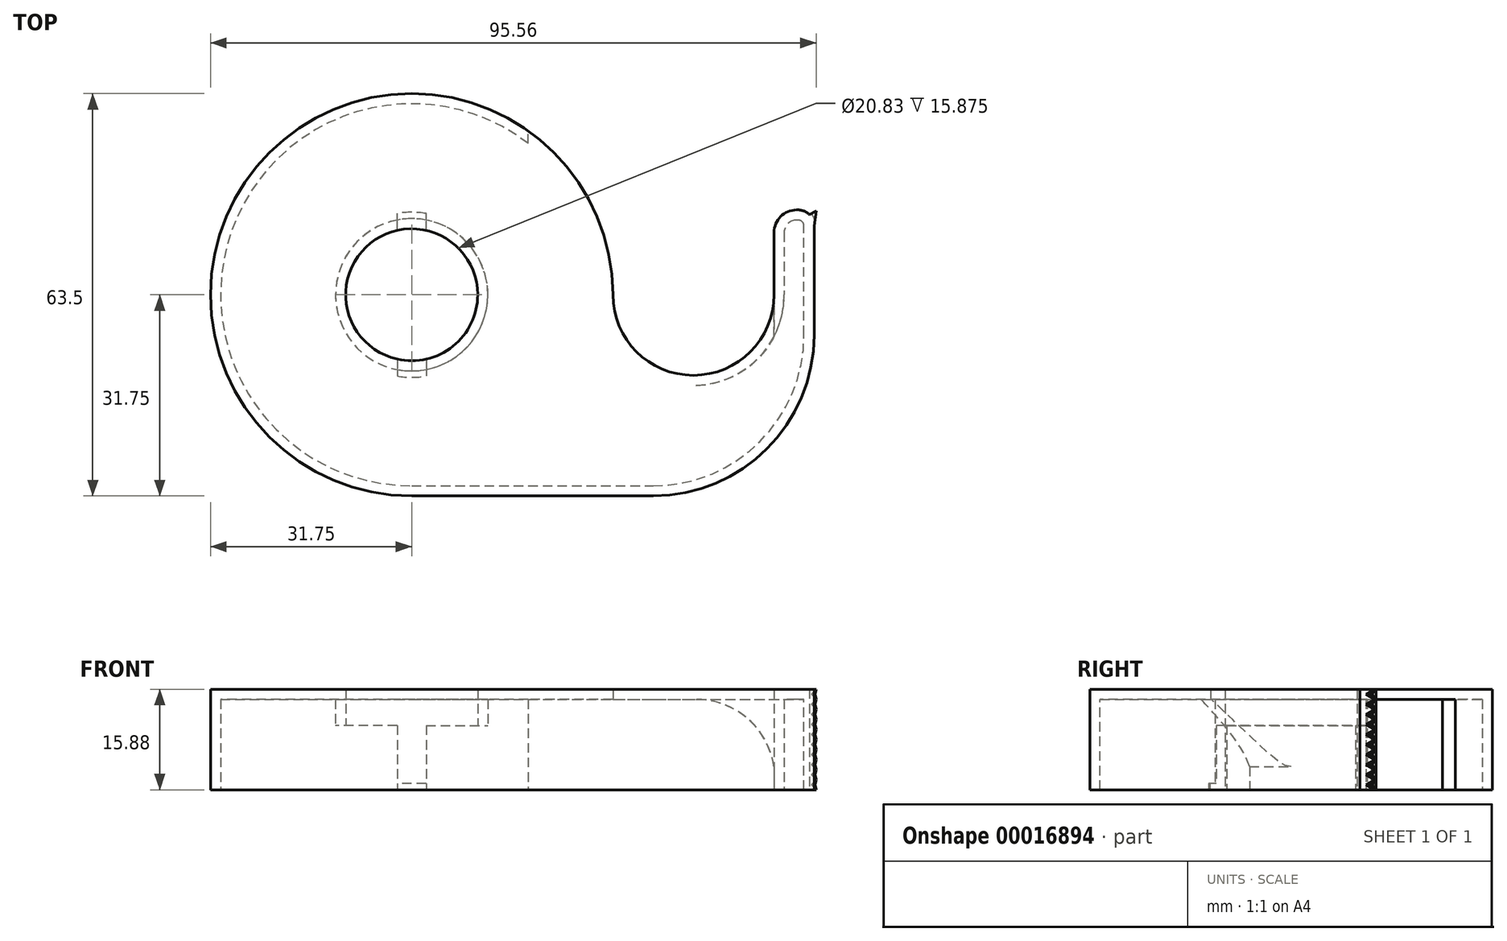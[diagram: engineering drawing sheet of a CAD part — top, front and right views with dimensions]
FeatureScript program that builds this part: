
annotation { "Feature Type Name" : "Feature", "Feature Type Description" : "" }
export const myFeature = defineFeature(function(context is Context, id is Id, definition is map)
    precondition{}
    {
        {
            var Q0;
            Q0=qCreatedBy(makeId("Top.planeOp"),FACE);
            var sketch = newSketch(context, id + "F0", { "sketchPlane" : qUnion([Q0])});
            skCircle(sketch, "E0", {"center": v(0, 0) * mm, "radius": 10.41 * mm});
            skArc(sketch, "E1", {"start": v(31.75, 0) * mm, "mid": v(-22.45, 22.45) * mm, "end": v(0, -31.75) * mm});
            skLineSegment(sketch, "E2", {"start": v(-31.75, 0) * mm, "end": v(31.75, 0) * mm, "construction": true});
            skLineSegment(sketch, "E3", {"start": v(0, -31.75) * mm, "end": v(38.1, -31.75) * mm});
            skLineSegment(sketch, "E4", {"start": v(63.5, -6.35) * mm, "end": v(63.5, 10.85) * mm});
            skLineSegment(sketch, "E5", {"start": v(60.96, 13.4) * mm, "end": v(60.73, 13.4) * mm});
            skLineSegment(sketch, "E6", {"start": v(57.17, 9.83) * mm, "end": v(57.17, 0) * mm});
            skArc(sketch, "E7", {"start": v(57.17, 0) * mm, "mid": v(44.46, -12.71) * mm, "end": v(31.75, 0) * mm});
            skLineSegment(sketch, "E8.trimOffspring", {"start": v(57.17, 13.4) * mm, "end": v(63.5, 13.4) * mm, "construction": true});
            skPoint(sketch, "E9.start.orphan", {"position": v(0, 10.41) * mm});
            skPoint(sketch, "E10.visualSharp", {"position": v(63.5, -31.75) * mm});
            skArc(sketch, "E10.filletArc", {"start": v(38.1, -31.75) * mm, "mid": v(56.06, -24.31) * mm, "end": v(63.5, -6.35) * mm});
            skPoint(sketch, "E11.visualSharp", {"position": v(63.5, 13.4) * mm});
            skArc(sketch, "E11.filletArc", {"start": v(62.76, 12.65) * mm, "mid": v(61.93, 13.2) * mm, "end": v(60.96, 13.4) * mm});
            skPoint(sketch, "E12.visualSharp", {"position": v(57.17, 13.4) * mm});
            skArc(sketch, "E12.filletArc", {"start": v(60.73, 13.4) * mm, "mid": v(58.21, 12.35) * mm, "end": v(57.17, 9.83) * mm});
            skLineSegment(sketch, "E13", {"start": v(63.5, 10.85) * mm, "end": v(63.8, 13.21) * mm});
            skLineSegment(sketch, "E14", {"start": v(63.8, 13.21) * mm, "end": v(62.76, 12.65) * mm});
            skSolve(sketch);
        }
        {
            var Q0;
            Q0=makeQuery(id+"F0.imprint","IMPRINT",FACE,{"disambiguationData":[TD([[makeQuery(id+"F0.imprint","IMPRINT",EDGE,{"derivedFrom":sQuery(id+"F0.wireOp",EDGE,"E0")}),-1.0]])]});
            extrude(context, id + "F1", {"entities" : qUnion([Q0]), "depth" : 15.88 * mm});
        }
        {
            var Q0;
            Q0=makeQuery(id+"F1.opExtrude","CAP_FACE",FACE,{"disambiguationData":[OSD([sQuery(id+"F0.wireOp",EDGE,"E0"),sQuery(id+"F0.wireOp",EDGE,"E1"),sQuery(id+"F0.wireOp",EDGE,"E3"),sQuery(id+"F0.wireOp",EDGE,"E4"),sQuery(id+"F0.wireOp",EDGE,"E5"),sQuery(id+"F0.wireOp",EDGE,"E6"),sQuery(id+"F0.wireOp",EDGE,"E7"),sQuery(id+"F0.wireOp",EDGE,"E10.filletArc")])],"isStart":true});
            shell(context, id + "F2", {"entities" : qUnion([Q0]), "thickness" : 1.6 * mm});
        }
        {
            var Q0;
            Q0=qCreatedBy(makeId("Front.planeOp"),FACE);
            cPlane(context, id + "F3", {"entities" : qUnion([Q0]), "cplaneType" : CPlaneType.OFFSET, "offset" : 38.1 * mm, "oppositeDirection" : true, "width" : 152.4 * mm, "height" : 152.4 * mm});
        }
        {
            var Q0;
            Q0=qCreatedBy(id+"F3.planeOp",FACE);
            var sketch = newSketch(context, id + "F4", { "sketchPlane" : qUnion([Q0])});
            skLineSegment(sketch, "E15.0", {"start": v(57.17, 15.88) * mm, "end": v(57.17, 0) * mm, "construction": true});
            skLineSegment(sketch, "E16.0", {"start": v(58.77, 14.27) * mm, "end": v(30.15, 14.27) * mm, "construction": true});
            skLineSegment(sketch, "E17.0", {"start": v(-30.15, 14.27) * mm, "end": v(30.15, 14.27) * mm, "construction": true});
            skLineSegment(sketch, "E18", {"start": v(18.4, 14.27) * mm, "end": v(18.4, -5.65) * mm});
            skLineSegment(sketch, "E19", {"start": v(18.4, -5.65) * mm, "end": v(57.17, -5.65) * mm});
            skLineSegment(sketch, "E20", {"start": v(18.4, 14.27) * mm, "end": v(44.86, 14.27) * mm});
            skArc(sketch, "E21", {"start": v(44.86, 14.27) * mm, "mid": v(53, 11.25) * mm, "end": v(57.17, 3.65) * mm});
            skLineSegment(sketch, "E22", {"start": v(57.17, 3.65) * mm, "end": v(57.17, -5.65) * mm});
            skSolve(sketch);
        }
        {
            var Q0;
            Q0 = qSketchRegion(id + "F4", true);
            extrude(context, id + "F5", {"entities" : qUnion([Q0]), "operationType" : NewBodyOperationType.REMOVE, "depth" : 53.45 * mm});
        }
        {
            var Q0;
            Q0=qCreatedBy(makeId("Top.planeOp"),FACE);
            var sketch = newSketch(context, id + "F6", { "sketchPlane" : qUnion([Q0])});
            skCircle(sketch, "E23.0", {"center": v(0, 0) * mm, "radius": 10.41 * mm});
            skLineSegment(sketch, "E24", {"start": v(-2.29, 12.7) * mm, "end": v(-2.29, 16.7) * mm});
            skLineSegment(sketch, "E25", {"start": v(-2.29, 16.7) * mm, "end": v(-16.67, 16.7) * mm});
            skLineSegment(sketch, "E26", {"start": v(0, 0) * mm, "end": v(0, 5.96) * mm});
            skLineSegment(sketch, "E27", {"start": v(0, 0) * mm, "end": v(-8.58, 0) * mm});
            skLineSegment(sketch, "E28", {"start": v(-16.67, 16.7) * mm, "end": v(-16.67, 0) * mm});
            skLineSegment(sketch, "E29", {"start": v(-2.29, 10.16) * mm, "end": v(-2.29, 12.7) * mm});
            skPoint(sketch, "E30.start.orphan", {"position": v(0, 10.41) * mm});
            skLineSegment(sketch, "E31.MirrorCS", {"start": v(2.29, 12.7) * mm, "end": v(2.29, 16.7) * mm});
            skLineSegment(sketch, "E32.MirrorCS", {"start": v(2.29, 16.7) * mm, "end": v(16.67, 16.7) * mm});
            skLineSegment(sketch, "E33.MirrorCS", {"start": v(16.67, 16.7) * mm, "end": v(16.67, 0) * mm});
            skLineSegment(sketch, "E34.MirrorCS", {"start": v(2.29, 10.16) * mm, "end": v(2.29, 12.7) * mm});
            skLineSegment(sketch, "E35.MirrorCS", {"start": v(-2.29, -12.7) * mm, "end": v(-2.29, -16.7) * mm});
            skLineSegment(sketch, "E36.MirrorCS", {"start": v(-2.29, -16.7) * mm, "end": v(-16.67, -16.7) * mm});
            skLineSegment(sketch, "E37.MirrorCS", {"start": v(-16.67, -16.7) * mm, "end": v(-16.67, 0) * mm});
            skLineSegment(sketch, "E38.MirrorCS", {"start": v(-2.29, -10.16) * mm, "end": v(-2.29, -12.7) * mm});
            skLineSegment(sketch, "E39.MirrorCS", {"start": v(16.67, -16.7) * mm, "end": v(16.67, 0) * mm});
            skLineSegment(sketch, "E40.MirrorCS", {"start": v(2.29, -16.7) * mm, "end": v(16.67, -16.7) * mm});
            skLineSegment(sketch, "E41.MirrorCS", {"start": v(2.29, -12.7) * mm, "end": v(2.29, -16.7) * mm});
            skLineSegment(sketch, "E42.MirrorCS", {"start": v(2.29, -10.16) * mm, "end": v(2.29, -12.7) * mm});
            skSolve(sketch);
        }
        {
            var Q0;
            Q0 = qSketchRegion(id + "F6", true);
            extrude(context, id + "F7", {"entities" : qUnion([Q0]), "operationType" : NewBodyOperationType.REMOVE, "depth" : 10.16 * mm});
        }
        {
            var Q0;
            {var subQ0=sQuery(id+"F0.wireOp",EDGE,"E0");var subQ1=sQuery(id+"F0.wireOp",EDGE,"E1");var subQ2=sQuery(id+"F0.wireOp",EDGE,"E3");var subQ3=sQuery(id+"F0.wireOp",EDGE,"E4");var subQ4=sQuery(id+"F0.wireOp",EDGE,"E5");var subQ5=sQuery(id+"F0.wireOp",EDGE,"E6");var subQ6=sQuery(id+"F0.wireOp",EDGE,"E7");var subQ7=sQuery(id+"F0.wireOp",EDGE,"E10.filletArc");Q0=makeQuery(id+"F7.boolean.opBoolean","SPLIT",FACE,{"disambiguationData":[TD([makeQuery(id+"F7.opExtrude","SWEPT_FACE",FACE,{"disambiguationData":[OSD([sQuery(id+"F6.wireOp",EDGE,"E35.MirrorCS"),sQuery(id+"F6.wireOp",EDGE,"E38.MirrorCS")])]})])],"derivedFrom":makeQuery(id+"F2.opShell","OFFSET_FACE",FACE,{"disambiguationData":[OSD([subQ0,subQ1,subQ2,subQ3,subQ4,subQ5,subQ6,subQ7]),TDD([makeQuery(id+"F1.opExtrude","CAP_FACE",FACE,{"disambiguationData":[OSD([subQ0,subQ1,subQ2,subQ3,subQ4,subQ5,subQ6,subQ7])],"isStart":true})])]})});}
            var sketch = newSketch(context, id + "F8", { "sketchPlane" : qUnion([Q0])});
            skLineSegment(sketch, "E43", {"start": v(-2.29, 11.8) * mm, "end": v(-2.29, 12.83) * mm});
            skLineSegment(sketch, "E44", {"start": v(2.29, 11.8) * mm, "end": v(2.29, 12.83) * mm});
            skArc(sketch, "E45.0", {"start": v(-2.29, 11.8) * mm, "mid": v(0, 12.01) * mm, "end": v(2.29, 11.8) * mm});
            skArc(sketch, "E46.0", {"start": v(-2.29, 12.83) * mm, "mid": v(0, 13.03) * mm, "end": v(2.29, 12.83) * mm});
            skLineSegment(sketch, "E47", {"start": v(0, 0) * mm, "end": v(-7.46, 0) * mm, "construction": true});
            skLineSegment(sketch, "E48.MirrorCS", {"start": v(2.29, -11.8) * mm, "end": v(2.29, -12.83) * mm});
            skArc(sketch, "E49.MirrorCS", {"start": v(-2.29, -12.83) * mm, "mid": v(0, -13.03) * mm, "end": v(2.29, -12.83) * mm});
            skLineSegment(sketch, "E50.MirrorCS", {"start": v(-2.29, -11.8) * mm, "end": v(-2.29, -12.83) * mm});
            skArc(sketch, "E51.MirrorCS", {"start": v(-2.29, -11.8) * mm, "mid": v(0, -12.01) * mm, "end": v(2.29, -11.8) * mm});
            skSolve(sketch);
        }
        {
            var Q0;
            Q0 = qSketchRegion(id + "F8", true);
            extrude(context, id + "F9", {"entities" : qUnion([Q0]), "operationType" : NewBodyOperationType.ADD, "oppositeDirection" : true, "depth" : 1.02 * mm});
        }
        {
            var Q0;
            Q0=makeQuery(id+"F1.opExtrude","SWEPT_FACE",FACE,{"disambiguationData":[OSD([sQuery(id+"F0.wireOp",EDGE,"E14")])]});
            var sketch = newSketch(context, id + "F10", { "sketchPlane" : qUnion([Q0])});
            skLineSegment(sketch, "E52", {"start": v(-62.5, 0) * mm, "end": v(-62.5, 1.59) * mm});
            skLineSegment(sketch, "E53", {"start": v(-62.5, 1.59) * mm, "end": v(-61.68, 0.8) * mm});
            skLineSegment(sketch, "E54", {"start": v(-61.68, 0.8) * mm, "end": v(-62.5, 0) * mm});
            skLineSegment(sketch, "E55.0.1.0", {"start": v(-62.5, 3.17) * mm, "end": v(-61.68, 2.38) * mm});
            skLineSegment(sketch, "E55.0.1.1", {"start": v(-61.68, 2.38) * mm, "end": v(-62.5, 1.59) * mm});
            skLineSegment(sketch, "E55.0.1.2", {"start": v(-62.5, 1.59) * mm, "end": v(-62.5, 3.18) * mm});
            skLineSegment(sketch, "E55.0.2.0", {"start": v(-62.5, 4.76) * mm, "end": v(-61.68, 3.97) * mm});
            skLineSegment(sketch, "E55.0.2.1", {"start": v(-61.68, 3.97) * mm, "end": v(-62.5, 3.18) * mm});
            skLineSegment(sketch, "E55.0.2.2", {"start": v(-62.5, 3.18) * mm, "end": v(-62.5, 4.76) * mm});
            skLineSegment(sketch, "E55.0.3.0", {"start": v(-62.5, 6.35) * mm, "end": v(-61.68, 5.56) * mm});
            skLineSegment(sketch, "E55.0.3.1", {"start": v(-61.68, 5.56) * mm, "end": v(-62.5, 4.76) * mm});
            skLineSegment(sketch, "E55.0.3.2", {"start": v(-62.5, 4.76) * mm, "end": v(-62.5, 6.35) * mm});
            skLineSegment(sketch, "E55.0.4.0", {"start": v(-62.5, 7.94) * mm, "end": v(-61.68, 7.14) * mm});
            skLineSegment(sketch, "E55.0.4.1", {"start": v(-61.68, 7.14) * mm, "end": v(-62.5, 6.35) * mm});
            skLineSegment(sketch, "E55.0.4.2", {"start": v(-62.5, 6.35) * mm, "end": v(-62.5, 7.94) * mm});
            skLineSegment(sketch, "E55.0.5.0", {"start": v(-62.5, 9.53) * mm, "end": v(-61.68, 8.73) * mm});
            skLineSegment(sketch, "E55.0.5.1", {"start": v(-61.68, 8.73) * mm, "end": v(-62.5, 7.94) * mm});
            skLineSegment(sketch, "E55.0.5.2", {"start": v(-62.5, 7.94) * mm, "end": v(-62.5, 9.53) * mm});
            skLineSegment(sketch, "E55.0.6.0", {"start": v(-62.5, 11.11) * mm, "end": v(-61.68, 10.32) * mm});
            skLineSegment(sketch, "E55.0.6.1", {"start": v(-61.68, 10.32) * mm, "end": v(-62.5, 9.53) * mm});
            skLineSegment(sketch, "E55.0.6.2", {"start": v(-62.5, 9.53) * mm, "end": v(-62.5, 11.11) * mm});
            skLineSegment(sketch, "E55.0.7.0", {"start": v(-62.5, 12.7) * mm, "end": v(-61.68, 11.9) * mm});
            skLineSegment(sketch, "E55.0.7.1", {"start": v(-61.68, 11.9) * mm, "end": v(-62.5, 11.11) * mm});
            skLineSegment(sketch, "E55.0.7.2", {"start": v(-62.5, 11.11) * mm, "end": v(-62.5, 12.7) * mm});
            skLineSegment(sketch, "E55.0.8.0", {"start": v(-62.5, 14.29) * mm, "end": v(-61.68, 13.5) * mm});
            skLineSegment(sketch, "E55.0.8.1", {"start": v(-61.68, 13.5) * mm, "end": v(-62.5, 12.7) * mm});
            skLineSegment(sketch, "E55.0.8.2", {"start": v(-62.5, 12.7) * mm, "end": v(-62.5, 14.29) * mm});
            skLineSegment(sketch, "E55.0.9.0", {"start": v(-62.5, 15.88) * mm, "end": v(-61.68, 15.08) * mm});
            skLineSegment(sketch, "E55.0.9.1", {"start": v(-61.68, 15.08) * mm, "end": v(-62.5, 14.29) * mm});
            skLineSegment(sketch, "E55.0.9.2", {"start": v(-62.5, 14.29) * mm, "end": v(-62.5, 15.88) * mm});
            skLineSegment(sketch, "E55.direction1", {"start": v(-62.5, 1.59) * mm, "end": v(-37.1, 1.59) * mm, "construction": true});
            skLineSegment(sketch, "E55.direction2", {"start": v(-62.5, 1.59) * mm, "end": v(-62.5, 3.17) * mm, "construction": true});
            skSolve(sketch);
        }
        {
            var Q0;
            Q0 = qSketchRegion(id + "F10", true);
            extrude(context, id + "F11", {"entities" : qUnion([Q0]), "operationType" : NewBodyOperationType.REMOVE, "oppositeDirection" : true, "depth" : 25.4 * mm});
        }
    });
